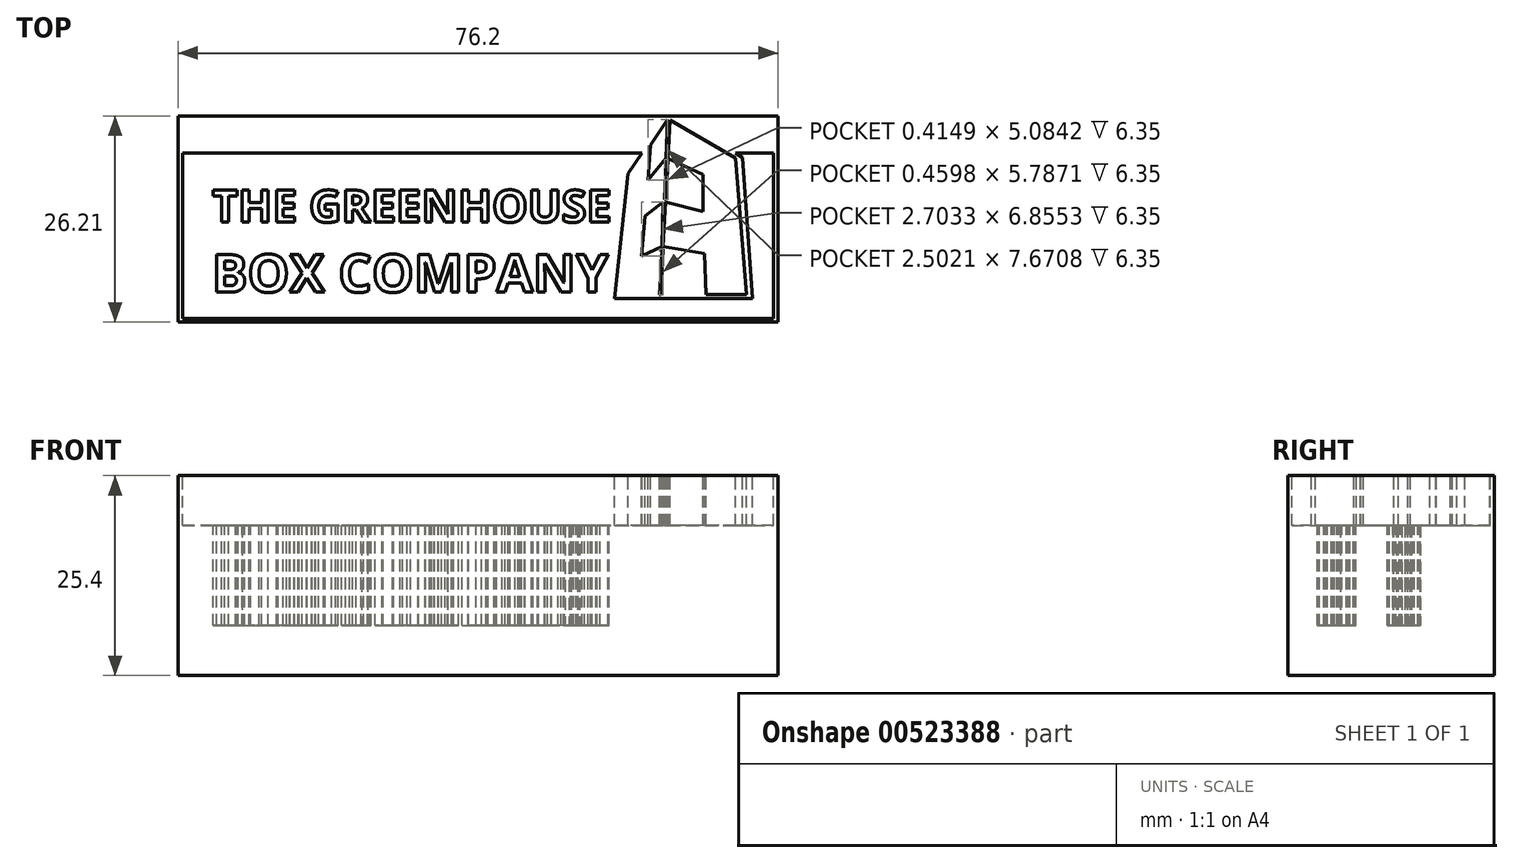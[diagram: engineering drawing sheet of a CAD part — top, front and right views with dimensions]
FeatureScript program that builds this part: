
annotation { "Feature Type Name" : "Feature", "Feature Type Description" : "" }
export const myFeature = defineFeature(function(context is Context, id is Id, definition is map)
    precondition{}
    {
        {
            var Q0;
            Q0=qCreatedBy(makeId("Top.planeOp"),FACE);
            var sketch = newSketch(context, id + "F0", { "sketchPlane" : qUnion([Q0])});
            skLineSegment(sketch, "E0", {"start": v(0.6, 21.46) * mm, "end": v(58.94, 21.46) * mm});
            skLineSegment(sketch, "E1", {"start": v(58.94, 21.46) * mm, "end": v(57.17, 18.86) * mm});
            skLineSegment(sketch, "E2", {"start": v(57.17, 18.86) * mm, "end": v(55.44, 3.02) * mm});
            skLineSegment(sketch, "E3", {"start": v(55.44, 3.02) * mm, "end": v(72.98, 3.02) * mm});
            skLineSegment(sketch, "E4", {"start": v(72.98, 3.02) * mm, "end": v(71.73, 20.92) * mm});
            skLineSegment(sketch, "E5", {"start": v(71.73, 20.92) * mm, "end": v(70.78, 21.48) * mm});
            skLineSegment(sketch, "E6", {"start": v(70.78, 21.48) * mm, "end": v(75.63, 21.48) * mm});
            skLineSegment(sketch, "E7", {"start": v(75.63, 21.48) * mm, "end": v(75.63, 0.5) * mm});
            skLineSegment(sketch, "E8", {"start": v(75.63, 0.5) * mm, "end": v(0.6, 0.5) * mm});
            skLineSegment(sketch, "E9", {"start": v(0.6, 0.5) * mm, "end": v(0.6, 21.46) * mm});
            skLineSegment(sketch, "E10", {"start": v(67.06, 3.49) * mm, "end": v(72.19, 3.49) * mm});
            skLineSegment(sketch, "E11", {"start": v(72.19, 3.49) * mm, "end": v(70.8, 20.87) * mm});
            skLineSegment(sketch, "E12", {"start": v(70.8, 20.87) * mm, "end": v(62.48, 25.7) * mm});
            skLineSegment(sketch, "E13", {"start": v(62.48, 25.7) * mm, "end": v(62.21, 20.76) * mm});
            skLineSegment(sketch, "E14", {"start": v(62.21, 20.76) * mm, "end": v(66.7, 18.78) * mm});
            skLineSegment(sketch, "E15", {"start": v(66.7, 18.78) * mm, "end": v(66.7, 14.08) * mm});
            skLineSegment(sketch, "E16", {"start": v(66.7, 14.08) * mm, "end": v(61.92, 15.26) * mm});
            skLineSegment(sketch, "E17", {"start": v(61.92, 15.26) * mm, "end": v(61.62, 9.6) * mm});
            skLineSegment(sketch, "E18", {"start": v(67.06, 3.49) * mm, "end": v(66.89, 8.71) * mm});
            skLineSegment(sketch, "E19", {"start": v(66.89, 8.71) * mm, "end": v(61.62, 9.6) * mm});
            skLineSegment(sketch, "E20", {"start": v(62, 20.84) * mm, "end": v(59.7, 18.08) * mm});
            skLineSegment(sketch, "E21", {"start": v(59.7, 18.08) * mm, "end": v(60, 22.48) * mm});
            skLineSegment(sketch, "E22", {"start": v(60, 22.48) * mm, "end": v(62.2, 25.75) * mm});
            skLineSegment(sketch, "E23", {"start": v(62.2, 25.75) * mm, "end": v(62, 20.84) * mm});
            skLineSegment(sketch, "E24", {"start": v(59.33, 13.5) * mm, "end": v(61.58, 15.26) * mm});
            skLineSegment(sketch, "E25", {"start": v(61.58, 15.26) * mm, "end": v(61.44, 9.6) * mm});
            skLineSegment(sketch, "E26", {"start": v(61.44, 9.6) * mm, "end": v(58.87, 8.4) * mm});
            skLineSegment(sketch, "E27", {"start": v(58.87, 8.4) * mm, "end": v(59.33, 13.5) * mm});
            skLineSegment(sketch, "E28", {"start": v(62, 20.66) * mm, "end": v(61.79, 15.58) * mm});
            skLineSegment(sketch, "E29", {"start": v(61.79, 15.58) * mm, "end": v(62, 15.58) * mm});
            skLineSegment(sketch, "E30", {"start": v(62, 15.58) * mm, "end": v(62.2, 20.65) * mm});
            skLineSegment(sketch, "E31", {"start": v(62.2, 20.65) * mm, "end": v(62, 20.66) * mm});
            skLineSegment(sketch, "E32", {"start": v(61.44, 9.25) * mm, "end": v(61.16, 3.5) * mm});
            skLineSegment(sketch, "E33", {"start": v(61.16, 3.5) * mm, "end": v(61.34, 3.48) * mm});
            skLineSegment(sketch, "E34", {"start": v(61.34, 3.48) * mm, "end": v(61.62, 9.27) * mm});
            skLineSegment(sketch, "E35", {"start": v(61.62, 9.27) * mm, "end": v(61.44, 9.25) * mm});
            skText(sketch, "E36", { "text": "THE GREENHOUSE", "fontName": "OpenSans-Bold.ttf"});
            skText(sketch, "E37", { "text": "BOX COMPANY\n", "fontName": "OpenSans-Bold.ttf"});
            skLineSegment(sketch, "E38.bottom", {"start": v(0, 26.21) * mm, "end": v(76.2, 26.21) * mm});
            skLineSegment(sketch, "E38.top", {"start": v(0, 0) * mm, "end": v(76.2, 0) * mm});
            skLineSegment(sketch, "E38.left", {"start": v(0, 26.21) * mm, "end": v(0, 0) * mm});
            skLineSegment(sketch, "E38.right", {"start": v(76.2, 26.21) * mm, "end": v(76.2, 0) * mm});
            const initialGuessF0  = {"E36": [0.00432, 0.0127, 1, 0, 0.0041], "E37": [0.00432, 0.00381, 1, 0, 0.00482]};
            skSetInitialGuess(sketch, initialGuessF0);
            skSolve(sketch);
        }
        {
            var Q0;
            Q0=makeQuery(id+"F0.imprint","IMPRINT",FACE,{"disambiguationData":[TD([[makeQuery(id+"F0.imprint","IMPRINT",EDGE,{"derivedFrom":sQuery(id+"F0.wireOp",EDGE,"E0")}),1.0]])]});
            var Q1;
            Q1=makeQuery(id+"F0.imprint","IMPRINT",FACE,{"disambiguationData":[TD([[makeQuery(id+"F0.imprint","IMPRINT",EDGE,{"derivedFrom":sQuery(id+"F0.wireOp",EDGE,"E36.sketch_text.stroke-82")}),-1.0]])]});
            var Q2;
            Q2=makeQuery(id+"F0.imprint","IMPRINT",FACE,{"disambiguationData":[TD([[makeQuery(id+"F0.imprint","IMPRINT",EDGE,{"derivedFrom":sQuery(id+"F0.wireOp",EDGE,"E37.sketch_text.stroke-74")}),1.0]])]});
            var Q3;
            Q3=makeQuery(id+"F0.imprint","IMPRINT",FACE,{"disambiguationData":[TD([[makeQuery(id+"F0.imprint","IMPRINT",EDGE,{"derivedFrom":sQuery(id+"F0.wireOp",EDGE,"E37.sketch_text.stroke-51")}),-1.0]])]});
            var Q4;
            Q4=makeQuery(id+"F0.imprint","IMPRINT",FACE,{"disambiguationData":[TD([[makeQuery(id+"F0.imprint","IMPRINT",EDGE,{"derivedFrom":sQuery(id+"F0.wireOp",EDGE,"E36.sketch_text.stroke-8")}),-1.0]])]});
            var Q5;
            Q5=makeQuery(id+"F0.imprint","IMPRINT",FACE,{"disambiguationData":[TD([[makeQuery(id+"F0.imprint","IMPRINT",EDGE,{"derivedFrom":sQuery(id+"F0.wireOp",EDGE,"E36.sketch_text.stroke-134")}),-1.0]])]});
            var Q6;
            Q6=makeQuery(id+"F0.imprint","IMPRINT",FACE,{"disambiguationData":[TD([[makeQuery(id+"F0.imprint","IMPRINT",EDGE,{"derivedFrom":sQuery(id+"F0.wireOp",EDGE,"E36.sketch_text.stroke-20")}),-1.0]])]});
            var Q7;
            Q7=makeQuery(id+"F0.imprint","IMPRINT",FACE,{"disambiguationData":[TD([[makeQuery(id+"F0.imprint","IMPRINT",EDGE,{"derivedFrom":sQuery(id+"F0.wireOp",EDGE,"E37.sketch_text.stroke-80")}),-1.0]])]});
            var Q8;
            Q8=makeQuery(id+"F0.imprint","IMPRINT",FACE,{"disambiguationData":[TD([[makeQuery(id+"F0.imprint","IMPRINT",EDGE,{"derivedFrom":sQuery(id+"F0.wireOp",EDGE,"E37.sketch_text.stroke-66")}),-1.0]])]});
            var Q9;
            Q9=makeQuery(id+"F0.imprint","IMPRINT",FACE,{"disambiguationData":[TD([[makeQuery(id+"F0.imprint","IMPRINT",EDGE,{"derivedFrom":sQuery(id+"F0.wireOp",EDGE,"E37.sketch_text.stroke-25")}),-1.0]])]});
            var Q10;
            Q10=makeQuery(id+"F0.imprint","IMPRINT",FACE,{"disambiguationData":[TD([[makeQuery(id+"F0.imprint","IMPRINT",EDGE,{"derivedFrom":sQuery(id+"F0.wireOp",EDGE,"E36.sketch_text.stroke-70")}),-1.0]])]});
            var Q11;
            Q11=makeQuery(id+"F0.imprint","IMPRINT",FACE,{"disambiguationData":[TD([[makeQuery(id+"F0.imprint","IMPRINT",EDGE,{"derivedFrom":sQuery(id+"F0.wireOp",EDGE,"E37.sketch_text.stroke-99")}),-1.0]])]});
            var Q12;
            Q12=makeQuery(id+"F0.imprint","IMPRINT",FACE,{"disambiguationData":[TD([[makeQuery(id+"F0.imprint","IMPRINT",EDGE,{"derivedFrom":sQuery(id+"F0.wireOp",EDGE,"E37.sketch_text.stroke-33")}),1.0]])]});
            var Q13;
            Q13=makeQuery(id+"F0.imprint","IMPRINT",FACE,{"disambiguationData":[TD([[makeQuery(id+"F0.imprint","IMPRINT",EDGE,{"derivedFrom":sQuery(id+"F0.wireOp",EDGE,"E36.sketch_text.stroke-32")}),-1.0]])]});
            var Q14;
            Q14=makeQuery(id+"F0.imprint","IMPRINT",FACE,{"disambiguationData":[TD([[makeQuery(id+"F0.imprint","IMPRINT",EDGE,{"derivedFrom":sQuery(id+"F0.wireOp",EDGE,"E24")}),-1.0]])]});
            var Q15;
            Q15=makeQuery(id+"F0.imprint","IMPRINT",FACE,{"disambiguationData":[TD([[makeQuery(id+"F0.imprint","IMPRINT",EDGE,{"derivedFrom":sQuery(id+"F0.wireOp",EDGE,"E36.sketch_text.stroke-108")}),-1.0]])]});
            var Q16;
            Q16=makeQuery(id+"F0.imprint","IMPRINT",FACE,{"disambiguationData":[TD([[makeQuery(id+"F0.imprint","IMPRINT",EDGE,{"derivedFrom":sQuery(id+"F0.wireOp",EDGE,"E37.sketch_text.stroke-115")}),-1.0]])]});
            var Q17;
            Q17=makeQuery(id+"F0.imprint","IMPRINT",FACE,{"disambiguationData":[TD([[makeQuery(id+"F0.imprint","IMPRINT",EDGE,{"derivedFrom":sQuery(id+"F0.wireOp",EDGE,"E37.sketch_text.stroke-19")}),1.0]])]});
            var Q18;
            Q18=makeQuery(id+"F0.imprint","IMPRINT",FACE,{"disambiguationData":[TD([[makeQuery(id+"F0.imprint","IMPRINT",EDGE,{"derivedFrom":sQuery(id+"F0.wireOp",EDGE,"E36.sketch_text.stroke-94")}),-1.0]])]});
            var Q19;
            Q19=makeQuery(id+"F0.imprint","IMPRINT",FACE,{"disambiguationData":[TD([[makeQuery(id+"F0.imprint","IMPRINT",EDGE,{"derivedFrom":sQuery(id+"F0.wireOp",EDGE,"E37.sketch_text.stroke-99")}),1.0]])]});
            var Q20;
            Q20=makeQuery(id+"F0.imprint","IMPRINT",FACE,{"disambiguationData":[TD([[makeQuery(id+"F0.imprint","IMPRINT",EDGE,{"derivedFrom":sQuery(id+"F0.wireOp",EDGE,"E36.sketch_text.stroke-51")}),-1.0]])]});
            var Q21;
            Q21=makeQuery(id+"F0.imprint","IMPRINT",FACE,{"disambiguationData":[TD([[makeQuery(id+"F0.imprint","IMPRINT",EDGE,{"derivedFrom":sQuery(id+"F0.wireOp",EDGE,"E37.sketch_text.stroke-39")}),-1.0]])]});
            var Q22;
            Q22=makeQuery(id+"F0.imprint","IMPRINT",FACE,{"disambiguationData":[TD([[makeQuery(id+"F0.imprint","IMPRINT",EDGE,{"derivedFrom":sQuery(id+"F0.wireOp",EDGE,"E37.sketch_text.stroke-12")}),1.0]])]});
            var Q23;
            Q23=makeQuery(id+"F0.imprint","IMPRINT",FACE,{"disambiguationData":[TD([[makeQuery(id+"F0.imprint","IMPRINT",EDGE,{"derivedFrom":sQuery(id+"F0.wireOp",EDGE,"E36.sketch_text.stroke-149")}),-1.0]])]});
            var Q24;
            Q24=makeQuery(id+"F0.imprint","IMPRINT",FACE,{"disambiguationData":[TD([[makeQuery(id+"F0.imprint","IMPRINT",EDGE,{"derivedFrom":sQuery(id+"F0.wireOp",EDGE,"E36.sketch_text.stroke-120")}),-1.0]])]});
            var Q25;
            Q25=makeQuery(id+"F0.imprint","IMPRINT",FACE,{"disambiguationData":[TD([[makeQuery(id+"F0.imprint","IMPRINT",EDGE,{"derivedFrom":sQuery(id+"F0.wireOp",EDGE,"E36.sketch_text.stroke-177")}),-1.0]])]});
            var Q26;
            Q26=makeQuery(id+"F0.imprint","IMPRINT",FACE,{"disambiguationData":[TD([[makeQuery(id+"F0.imprint","IMPRINT",EDGE,{"derivedFrom":sQuery(id+"F0.wireOp",EDGE,"E36.sketch_text.stroke-128")}),1.0]])]});
            var Q27;
            Q27=makeQuery(id+"F0.imprint","IMPRINT",FACE,{"disambiguationData":[TD([[makeQuery(id+"F0.imprint","IMPRINT",EDGE,{"derivedFrom":sQuery(id+"F0.wireOp",EDGE,"E37.sketch_text.stroke-141")}),-1.0]])]});
            var Q28;
            Q28=makeQuery(id+"F0.imprint","IMPRINT",FACE,{"disambiguationData":[TD([[makeQuery(id+"F0.imprint","IMPRINT",EDGE,{"derivedFrom":sQuery(id+"F0.wireOp",EDGE,"E37.sketch_text.stroke-123")}),1.0]])]});
            var Q29;
            Q29=makeQuery(id+"F0.imprint","IMPRINT",FACE,{"disambiguationData":[TD([[makeQuery(id+"F0.imprint","IMPRINT",EDGE,{"derivedFrom":sQuery(id+"F0.wireOp",EDGE,"E36.sketch_text.stroke-0")}),-1.0]])]});
            var Q30;
            Q30=makeQuery(id+"F0.imprint","IMPRINT",FACE,{"disambiguationData":[TD([[makeQuery(id+"F0.imprint","IMPRINT",EDGE,{"derivedFrom":sQuery(id+"F0.wireOp",EDGE,"E37.sketch_text.stroke-127")}),-1.0]])]});
            var Q31;
            Q31=makeQuery(id+"F0.imprint","IMPRINT",FACE,{"disambiguationData":[TD([[makeQuery(id+"F0.imprint","IMPRINT",EDGE,{"derivedFrom":sQuery(id+"F0.wireOp",EDGE,"E28")}),1.0]])]});
            var Q32;
            Q32=makeQuery(id+"F0.imprint","IMPRINT",FACE,{"disambiguationData":[TD([[makeQuery(id+"F0.imprint","IMPRINT",EDGE,{"derivedFrom":sQuery(id+"F0.wireOp",EDGE,"E36.sketch_text.stroke-51")}),1.0]])]});
            var Q33;
            Q33=makeQuery(id+"F0.imprint","IMPRINT",FACE,{"disambiguationData":[TD([[makeQuery(id+"F0.imprint","IMPRINT",EDGE,{"derivedFrom":sQuery(id+"F0.wireOp",EDGE,"E32")}),1.0]])]});
            var Q34;
            Q34=makeQuery(id+"F0.imprint","IMPRINT",FACE,{"disambiguationData":[TD([[makeQuery(id+"F0.imprint","IMPRINT",EDGE,{"derivedFrom":sQuery(id+"F0.wireOp",EDGE,"E10")}),1.0]])]});
            var Q35;
            Q35=makeQuery(id+"F0.imprint","IMPRINT",FACE,{"disambiguationData":[TD([[makeQuery(id+"F0.imprint","IMPRINT",EDGE,{"derivedFrom":sQuery(id+"F0.wireOp",EDGE,"E20")}),-1.0]])]});
            var Q36;
            Q36=makeQuery(id+"F0.imprint","IMPRINT",FACE,{"disambiguationData":[TD([[makeQuery(id+"F0.imprint","IMPRINT",EDGE,{"derivedFrom":sQuery(id+"F0.wireOp",EDGE,"E37.sketch_text.stroke-0")}),-1.0]])]});
            var Q37;
            Q37=makeQuery(id+"F0.imprint","IMPRINT",FACE,{"disambiguationData":[TD([[makeQuery(id+"F0.imprint","IMPRINT",EDGE,{"derivedFrom":sQuery(id+"F0.wireOp",EDGE,"E0")}),-1.0]])]});
            extrude(context, id + "F1", {"entities" : qUnion([Q0, Q1, Q2, Q3, Q4, Q5, Q6, Q7, Q8, Q9, Q10, Q11, Q12, Q13, Q14, Q15, Q16, Q17, Q18, Q19, Q20, Q21, Q22, Q23, Q24, Q25, Q26, Q27, Q28, Q29, Q30, Q31, Q32, Q33, Q34, Q35, Q36, Q37]), "oppositeDirection" : true, "depth" : 25.4 * mm, "offsetDistance" : 25.4 * mm});
        }
        {
            var Q0;
            Q0=makeQuery(id+"F0.imprint","IMPRINT",FACE,{"disambiguationData":[TD([[makeQuery(id+"F0.imprint","IMPRINT",EDGE,{"derivedFrom":sQuery(id+"F0.wireOp",EDGE,"E0")}),-1.0]])]});
            var Q1;
            Q1=makeQuery(id+"F0.imprint","IMPRINT",FACE,{"disambiguationData":[TD([[makeQuery(id+"F0.imprint","IMPRINT",EDGE,{"derivedFrom":sQuery(id+"F0.wireOp",EDGE,"E36.sketch_text.stroke-51")}),-1.0]])]});
            var Q2;
            Q2=makeQuery(id+"F0.imprint","IMPRINT",FACE,{"disambiguationData":[TD([[makeQuery(id+"F0.imprint","IMPRINT",EDGE,{"derivedFrom":sQuery(id+"F0.wireOp",EDGE,"E36.sketch_text.stroke-94")}),-1.0]])]});
            var Q3;
            Q3=makeQuery(id+"F0.imprint","IMPRINT",FACE,{"disambiguationData":[TD([[makeQuery(id+"F0.imprint","IMPRINT",EDGE,{"derivedFrom":sQuery(id+"F0.wireOp",EDGE,"E36.sketch_text.stroke-8")}),-1.0]])]});
            var Q4;
            Q4=makeQuery(id+"F0.imprint","IMPRINT",FACE,{"disambiguationData":[TD([[makeQuery(id+"F0.imprint","IMPRINT",EDGE,{"derivedFrom":sQuery(id+"F0.wireOp",EDGE,"E36.sketch_text.stroke-70")}),-1.0]])]});
            var Q5;
            Q5=makeQuery(id+"F0.imprint","IMPRINT",FACE,{"disambiguationData":[TD([[makeQuery(id+"F0.imprint","IMPRINT",EDGE,{"derivedFrom":sQuery(id+"F0.wireOp",EDGE,"E36.sketch_text.stroke-20")}),-1.0]])]});
            var Q6;
            Q6=makeQuery(id+"F0.imprint","IMPRINT",FACE,{"disambiguationData":[TD([[makeQuery(id+"F0.imprint","IMPRINT",EDGE,{"derivedFrom":sQuery(id+"F0.wireOp",EDGE,"E36.sketch_text.stroke-108")}),-1.0]])]});
            var Q7;
            Q7=makeQuery(id+"F0.imprint","IMPRINT",FACE,{"disambiguationData":[TD([[makeQuery(id+"F0.imprint","IMPRINT",EDGE,{"derivedFrom":sQuery(id+"F0.wireOp",EDGE,"E36.sketch_text.stroke-82")}),-1.0]])]});
            var Q8;
            Q8=makeQuery(id+"F0.imprint","IMPRINT",FACE,{"disambiguationData":[TD([[makeQuery(id+"F0.imprint","IMPRINT",EDGE,{"derivedFrom":sQuery(id+"F0.wireOp",EDGE,"E36.sketch_text.stroke-32")}),-1.0]])]});
            var Q9;
            Q9=makeQuery(id+"F0.imprint","IMPRINT",FACE,{"disambiguationData":[TD([[makeQuery(id+"F0.imprint","IMPRINT",EDGE,{"derivedFrom":sQuery(id+"F0.wireOp",EDGE,"E36.sketch_text.stroke-51")}),1.0]])]});
            var Q10;
            Q10=makeQuery(id+"F0.imprint","IMPRINT",FACE,{"disambiguationData":[TD([[makeQuery(id+"F0.imprint","IMPRINT",EDGE,{"derivedFrom":sQuery(id+"F0.wireOp",EDGE,"E36.sketch_text.stroke-0")}),-1.0]])]});
            var Q11;
            Q11=makeQuery(id+"F0.imprint","IMPRINT",FACE,{"disambiguationData":[TD([[makeQuery(id+"F0.imprint","IMPRINT",EDGE,{"derivedFrom":sQuery(id+"F0.wireOp",EDGE,"E37.sketch_text.stroke-0")}),-1.0]])]});
            var Q12;
            Q12=makeQuery(id+"F0.imprint","IMPRINT",FACE,{"disambiguationData":[TD([[makeQuery(id+"F0.imprint","IMPRINT",EDGE,{"derivedFrom":sQuery(id+"F0.wireOp",EDGE,"E37.sketch_text.stroke-19")}),1.0]])]});
            var Q13;
            Q13=makeQuery(id+"F0.imprint","IMPRINT",FACE,{"disambiguationData":[TD([[makeQuery(id+"F0.imprint","IMPRINT",EDGE,{"derivedFrom":sQuery(id+"F0.wireOp",EDGE,"E37.sketch_text.stroke-33")}),1.0]])]});
            var Q14;
            Q14=makeQuery(id+"F0.imprint","IMPRINT",FACE,{"disambiguationData":[TD([[makeQuery(id+"F0.imprint","IMPRINT",EDGE,{"derivedFrom":sQuery(id+"F0.wireOp",EDGE,"E37.sketch_text.stroke-66")}),-1.0]])]});
            var Q15;
            Q15=makeQuery(id+"F0.imprint","IMPRINT",FACE,{"disambiguationData":[TD([[makeQuery(id+"F0.imprint","IMPRINT",EDGE,{"derivedFrom":sQuery(id+"F0.wireOp",EDGE,"E37.sketch_text.stroke-74")}),1.0]])]});
            var Q16;
            Q16=makeQuery(id+"F0.imprint","IMPRINT",FACE,{"disambiguationData":[TD([[makeQuery(id+"F0.imprint","IMPRINT",EDGE,{"derivedFrom":sQuery(id+"F0.wireOp",EDGE,"E37.sketch_text.stroke-99")}),1.0]])]});
            var Q17;
            Q17=makeQuery(id+"F0.imprint","IMPRINT",FACE,{"disambiguationData":[TD([[makeQuery(id+"F0.imprint","IMPRINT",EDGE,{"derivedFrom":sQuery(id+"F0.wireOp",EDGE,"E37.sketch_text.stroke-51")}),-1.0]])]});
            var Q18;
            Q18=makeQuery(id+"F0.imprint","IMPRINT",FACE,{"disambiguationData":[TD([[makeQuery(id+"F0.imprint","IMPRINT",EDGE,{"derivedFrom":sQuery(id+"F0.wireOp",EDGE,"E37.sketch_text.stroke-25")}),-1.0]])]});
            var Q19;
            Q19=makeQuery(id+"F0.imprint","IMPRINT",FACE,{"disambiguationData":[TD([[makeQuery(id+"F0.imprint","IMPRINT",EDGE,{"derivedFrom":sQuery(id+"F0.wireOp",EDGE,"E37.sketch_text.stroke-80")}),-1.0]])]});
            var Q20;
            Q20=makeQuery(id+"F0.imprint","IMPRINT",FACE,{"disambiguationData":[TD([[makeQuery(id+"F0.imprint","IMPRINT",EDGE,{"derivedFrom":sQuery(id+"F0.wireOp",EDGE,"E37.sketch_text.stroke-39")}),-1.0]])]});
            var Q21;
            Q21=makeQuery(id+"F0.imprint","IMPRINT",FACE,{"disambiguationData":[TD([[makeQuery(id+"F0.imprint","IMPRINT",EDGE,{"derivedFrom":sQuery(id+"F0.wireOp",EDGE,"E37.sketch_text.stroke-99")}),-1.0]])]});
            var Q22;
            Q22=makeQuery(id+"F0.imprint","IMPRINT",FACE,{"disambiguationData":[TD([[makeQuery(id+"F0.imprint","IMPRINT",EDGE,{"derivedFrom":sQuery(id+"F0.wireOp",EDGE,"E37.sketch_text.stroke-12")}),1.0]])]});
            var Q23;
            Q23=makeQuery(id+"F0.imprint","IMPRINT",FACE,{"disambiguationData":[TD([[makeQuery(id+"F0.imprint","IMPRINT",EDGE,{"derivedFrom":sQuery(id+"F0.wireOp",EDGE,"E36.sketch_text.stroke-177")}),-1.0]])]});
            var Q24;
            Q24=makeQuery(id+"F0.imprint","IMPRINT",FACE,{"disambiguationData":[TD([[makeQuery(id+"F0.imprint","IMPRINT",EDGE,{"derivedFrom":sQuery(id+"F0.wireOp",EDGE,"E36.sketch_text.stroke-134")}),-1.0]])]});
            var Q25;
            Q25=makeQuery(id+"F0.imprint","IMPRINT",FACE,{"disambiguationData":[TD([[makeQuery(id+"F0.imprint","IMPRINT",EDGE,{"derivedFrom":sQuery(id+"F0.wireOp",EDGE,"E36.sketch_text.stroke-149")}),-1.0]])]});
            var Q26;
            Q26=makeQuery(id+"F0.imprint","IMPRINT",FACE,{"disambiguationData":[TD([[makeQuery(id+"F0.imprint","IMPRINT",EDGE,{"derivedFrom":sQuery(id+"F0.wireOp",EDGE,"E36.sketch_text.stroke-120")}),-1.0]])]});
            var Q27;
            Q27=makeQuery(id+"F0.imprint","IMPRINT",FACE,{"disambiguationData":[TD([[makeQuery(id+"F0.imprint","IMPRINT",EDGE,{"derivedFrom":sQuery(id+"F0.wireOp",EDGE,"E36.sketch_text.stroke-128")}),1.0]])]});
            var Q28;
            Q28=makeQuery(id+"F0.imprint","IMPRINT",FACE,{"disambiguationData":[TD([[makeQuery(id+"F0.imprint","IMPRINT",EDGE,{"derivedFrom":sQuery(id+"F0.wireOp",EDGE,"E37.sketch_text.stroke-141")}),-1.0]])]});
            var Q29;
            Q29=makeQuery(id+"F0.imprint","IMPRINT",FACE,{"disambiguationData":[TD([[makeQuery(id+"F0.imprint","IMPRINT",EDGE,{"derivedFrom":sQuery(id+"F0.wireOp",EDGE,"E37.sketch_text.stroke-123")}),1.0]])]});
            var Q30;
            Q30=makeQuery(id+"F0.imprint","IMPRINT",FACE,{"disambiguationData":[TD([[makeQuery(id+"F0.imprint","IMPRINT",EDGE,{"derivedFrom":sQuery(id+"F0.wireOp",EDGE,"E37.sketch_text.stroke-127")}),-1.0]])]});
            var Q31;
            Q31=makeQuery(id+"F0.imprint","IMPRINT",FACE,{"disambiguationData":[TD([[makeQuery(id+"F0.imprint","IMPRINT",EDGE,{"derivedFrom":sQuery(id+"F0.wireOp",EDGE,"E37.sketch_text.stroke-115")}),-1.0]])]});
            extrude(context, id + "F2", {"entities" : qUnion([Q0, Q1, Q2, Q3, Q4, Q5, Q6, Q7, Q8, Q9, Q10, Q11, Q12, Q13, Q14, Q15, Q16, Q17, Q18, Q19, Q20, Q21, Q22, Q23, Q24, Q25, Q26, Q27, Q28, Q29, Q30, Q31]), "operationType" : NewBodyOperationType.REMOVE, "oppositeDirection" : true, "depth" : 6.35 * mm, "offsetDistance" : 25.4 * mm});
        }
        {
            var Q0;
            Q0=makeQuery(id+"F0.imprint","IMPRINT",FACE,{"disambiguationData":[TD([[makeQuery(id+"F0.imprint","IMPRINT",EDGE,{"derivedFrom":sQuery(id+"F0.wireOp",EDGE,"E36.sketch_text.stroke-0")}),-1.0]])]});
            var Q1;
            Q1=makeQuery(id+"F0.imprint","IMPRINT",FACE,{"disambiguationData":[TD([[makeQuery(id+"F0.imprint","IMPRINT",EDGE,{"derivedFrom":sQuery(id+"F0.wireOp",EDGE,"E36.sketch_text.stroke-8")}),-1.0]])]});
            var Q2;
            Q2=makeQuery(id+"F0.imprint","IMPRINT",FACE,{"disambiguationData":[TD([[makeQuery(id+"F0.imprint","IMPRINT",EDGE,{"derivedFrom":sQuery(id+"F0.wireOp",EDGE,"E36.sketch_text.stroke-20")}),-1.0]])]});
            var Q3;
            Q3=makeQuery(id+"F0.imprint","IMPRINT",FACE,{"disambiguationData":[TD([[makeQuery(id+"F0.imprint","IMPRINT",EDGE,{"derivedFrom":sQuery(id+"F0.wireOp",EDGE,"E36.sketch_text.stroke-32")}),-1.0]])]});
            var Q4;
            Q4=makeQuery(id+"F0.imprint","IMPRINT",FACE,{"disambiguationData":[TD([[makeQuery(id+"F0.imprint","IMPRINT",EDGE,{"derivedFrom":sQuery(id+"F0.wireOp",EDGE,"E36.sketch_text.stroke-51")}),-1.0]])]});
            var Q5;
            Q5=makeQuery(id+"F0.imprint","IMPRINT",FACE,{"disambiguationData":[TD([[makeQuery(id+"F0.imprint","IMPRINT",EDGE,{"derivedFrom":sQuery(id+"F0.wireOp",EDGE,"E36.sketch_text.stroke-70")}),-1.0]])]});
            var Q6;
            Q6=makeQuery(id+"F0.imprint","IMPRINT",FACE,{"disambiguationData":[TD([[makeQuery(id+"F0.imprint","IMPRINT",EDGE,{"derivedFrom":sQuery(id+"F0.wireOp",EDGE,"E36.sketch_text.stroke-82")}),-1.0]])]});
            var Q7;
            Q7=makeQuery(id+"F0.imprint","IMPRINT",FACE,{"disambiguationData":[TD([[makeQuery(id+"F0.imprint","IMPRINT",EDGE,{"derivedFrom":sQuery(id+"F0.wireOp",EDGE,"E37.sketch_text.stroke-0")}),-1.0]])]});
            var Q8;
            Q8=makeQuery(id+"F0.imprint","IMPRINT",FACE,{"disambiguationData":[TD([[makeQuery(id+"F0.imprint","IMPRINT",EDGE,{"derivedFrom":sQuery(id+"F0.wireOp",EDGE,"E37.sketch_text.stroke-25")}),-1.0]])]});
            var Q9;
            Q9=makeQuery(id+"F0.imprint","IMPRINT",FACE,{"disambiguationData":[TD([[makeQuery(id+"F0.imprint","IMPRINT",EDGE,{"derivedFrom":sQuery(id+"F0.wireOp",EDGE,"E37.sketch_text.stroke-39")}),-1.0]])]});
            var Q10;
            Q10=makeQuery(id+"F0.imprint","IMPRINT",FACE,{"disambiguationData":[TD([[makeQuery(id+"F0.imprint","IMPRINT",EDGE,{"derivedFrom":sQuery(id+"F0.wireOp",EDGE,"E37.sketch_text.stroke-51")}),-1.0]])]});
            var Q11;
            Q11=makeQuery(id+"F0.imprint","IMPRINT",FACE,{"disambiguationData":[TD([[makeQuery(id+"F0.imprint","IMPRINT",EDGE,{"derivedFrom":sQuery(id+"F0.wireOp",EDGE,"E37.sketch_text.stroke-66")}),-1.0]])]});
            var Q12;
            Q12=makeQuery(id+"F0.imprint","IMPRINT",FACE,{"disambiguationData":[TD([[makeQuery(id+"F0.imprint","IMPRINT",EDGE,{"derivedFrom":sQuery(id+"F0.wireOp",EDGE,"E37.sketch_text.stroke-80")}),-1.0]])]});
            var Q13;
            Q13=makeQuery(id+"F0.imprint","IMPRINT",FACE,{"disambiguationData":[TD([[makeQuery(id+"F0.imprint","IMPRINT",EDGE,{"derivedFrom":sQuery(id+"F0.wireOp",EDGE,"E36.sketch_text.stroke-94")}),-1.0]])]});
            var Q14;
            Q14=makeQuery(id+"F0.imprint","IMPRINT",FACE,{"disambiguationData":[TD([[makeQuery(id+"F0.imprint","IMPRINT",EDGE,{"derivedFrom":sQuery(id+"F0.wireOp",EDGE,"E36.sketch_text.stroke-108")}),-1.0]])]});
            var Q15;
            Q15=makeQuery(id+"F0.imprint","IMPRINT",FACE,{"disambiguationData":[TD([[makeQuery(id+"F0.imprint","IMPRINT",EDGE,{"derivedFrom":sQuery(id+"F0.wireOp",EDGE,"E36.sketch_text.stroke-120")}),-1.0]])]});
            var Q16;
            Q16=makeQuery(id+"F0.imprint","IMPRINT",FACE,{"disambiguationData":[TD([[makeQuery(id+"F0.imprint","IMPRINT",EDGE,{"derivedFrom":sQuery(id+"F0.wireOp",EDGE,"E37.sketch_text.stroke-99")}),-1.0]])]});
            var Q17;
            Q17=makeQuery(id+"F0.imprint","IMPRINT",FACE,{"disambiguationData":[TD([[makeQuery(id+"F0.imprint","IMPRINT",EDGE,{"derivedFrom":sQuery(id+"F0.wireOp",EDGE,"E37.sketch_text.stroke-115")}),-1.0]])]});
            var Q18;
            Q18=makeQuery(id+"F0.imprint","IMPRINT",FACE,{"disambiguationData":[TD([[makeQuery(id+"F0.imprint","IMPRINT",EDGE,{"derivedFrom":sQuery(id+"F0.wireOp",EDGE,"E37.sketch_text.stroke-127")}),-1.0]])]});
            var Q19;
            Q19=makeQuery(id+"F0.imprint","IMPRINT",FACE,{"disambiguationData":[TD([[makeQuery(id+"F0.imprint","IMPRINT",EDGE,{"derivedFrom":sQuery(id+"F0.wireOp",EDGE,"E37.sketch_text.stroke-141")}),-1.0]])]});
            var Q20;
            Q20=makeQuery(id+"F0.imprint","IMPRINT",FACE,{"disambiguationData":[TD([[makeQuery(id+"F0.imprint","IMPRINT",EDGE,{"derivedFrom":sQuery(id+"F0.wireOp",EDGE,"E36.sketch_text.stroke-134")}),-1.0]])]});
            var Q21;
            Q21=makeQuery(id+"F0.imprint","IMPRINT",FACE,{"disambiguationData":[TD([[makeQuery(id+"F0.imprint","IMPRINT",EDGE,{"derivedFrom":sQuery(id+"F0.wireOp",EDGE,"E36.sketch_text.stroke-149")}),-1.0]])]});
            var Q22;
            Q22=makeQuery(id+"F0.imprint","IMPRINT",FACE,{"disambiguationData":[TD([[makeQuery(id+"F0.imprint","IMPRINT",EDGE,{"derivedFrom":sQuery(id+"F0.wireOp",EDGE,"E36.sketch_text.stroke-177")}),-1.0]])]});
            extrude(context, id + "F3", {"entities" : qUnion([Q0, Q1, Q2, Q3, Q4, Q5, Q6, Q7, Q8, Q9, Q10, Q11, Q12, Q13, Q14, Q15, Q16, Q17, Q18, Q19, Q20, Q21, Q22]), "operationType" : NewBodyOperationType.REMOVE, "oppositeDirection" : true, "depth" : 19.05 * mm, "offsetDistance" : 25.4 * mm});
        }
        {
            var Q0;
            Q0=makeQuery(id+"F0.imprint","IMPRINT",FACE,{"disambiguationData":[TD([[makeQuery(id+"F0.imprint","IMPRINT",EDGE,{"derivedFrom":sQuery(id+"F0.wireOp",EDGE,"E10")}),1.0]])]});
            var Q1;
            Q1=makeQuery(id+"F0.imprint","IMPRINT",FACE,{"disambiguationData":[TD([[makeQuery(id+"F0.imprint","IMPRINT",EDGE,{"derivedFrom":sQuery(id+"F0.wireOp",EDGE,"E20")}),-1.0]])]});
            var Q2;
            Q2=makeQuery(id+"F0.imprint","IMPRINT",FACE,{"disambiguationData":[TD([[makeQuery(id+"F0.imprint","IMPRINT",EDGE,{"derivedFrom":sQuery(id+"F0.wireOp",EDGE,"E24")}),-1.0]])]});
            var Q3;
            Q3=makeQuery(id+"F0.imprint","IMPRINT",FACE,{"disambiguationData":[TD([[makeQuery(id+"F0.imprint","IMPRINT",EDGE,{"derivedFrom":sQuery(id+"F0.wireOp",EDGE,"E32")}),1.0]])]});
            var Q4;
            Q4=makeQuery(id+"F0.imprint","IMPRINT",FACE,{"disambiguationData":[TD([[makeQuery(id+"F0.imprint","IMPRINT",EDGE,{"derivedFrom":sQuery(id+"F0.wireOp",EDGE,"E28")}),1.0]])]});
            extrude(context, id + "F4", {"entities" : qUnion([Q0, Q1, Q2, Q3, Q4]), "operationType" : NewBodyOperationType.REMOVE, "oppositeDirection" : true, "depth" : 6.35 * mm, "offsetDistance" : 25.4 * mm});
        }
        {
            var Q0;
            Q0=makeQuery(id+"F0.imprint","IMPRINT",FACE,{"disambiguationData":[TD([[makeQuery(id+"F0.imprint","IMPRINT",EDGE,{"derivedFrom":sQuery(id+"F0.wireOp",EDGE,"E0")}),-1.0]])]});
            extrude(context, id + "F5", {"entities" : qUnion([Q0]), "operationType" : NewBodyOperationType.REMOVE, "oppositeDirection" : true, "depth" : 2.54 * mm, "offsetDistance" : 25.4 * mm});
        }
    });
